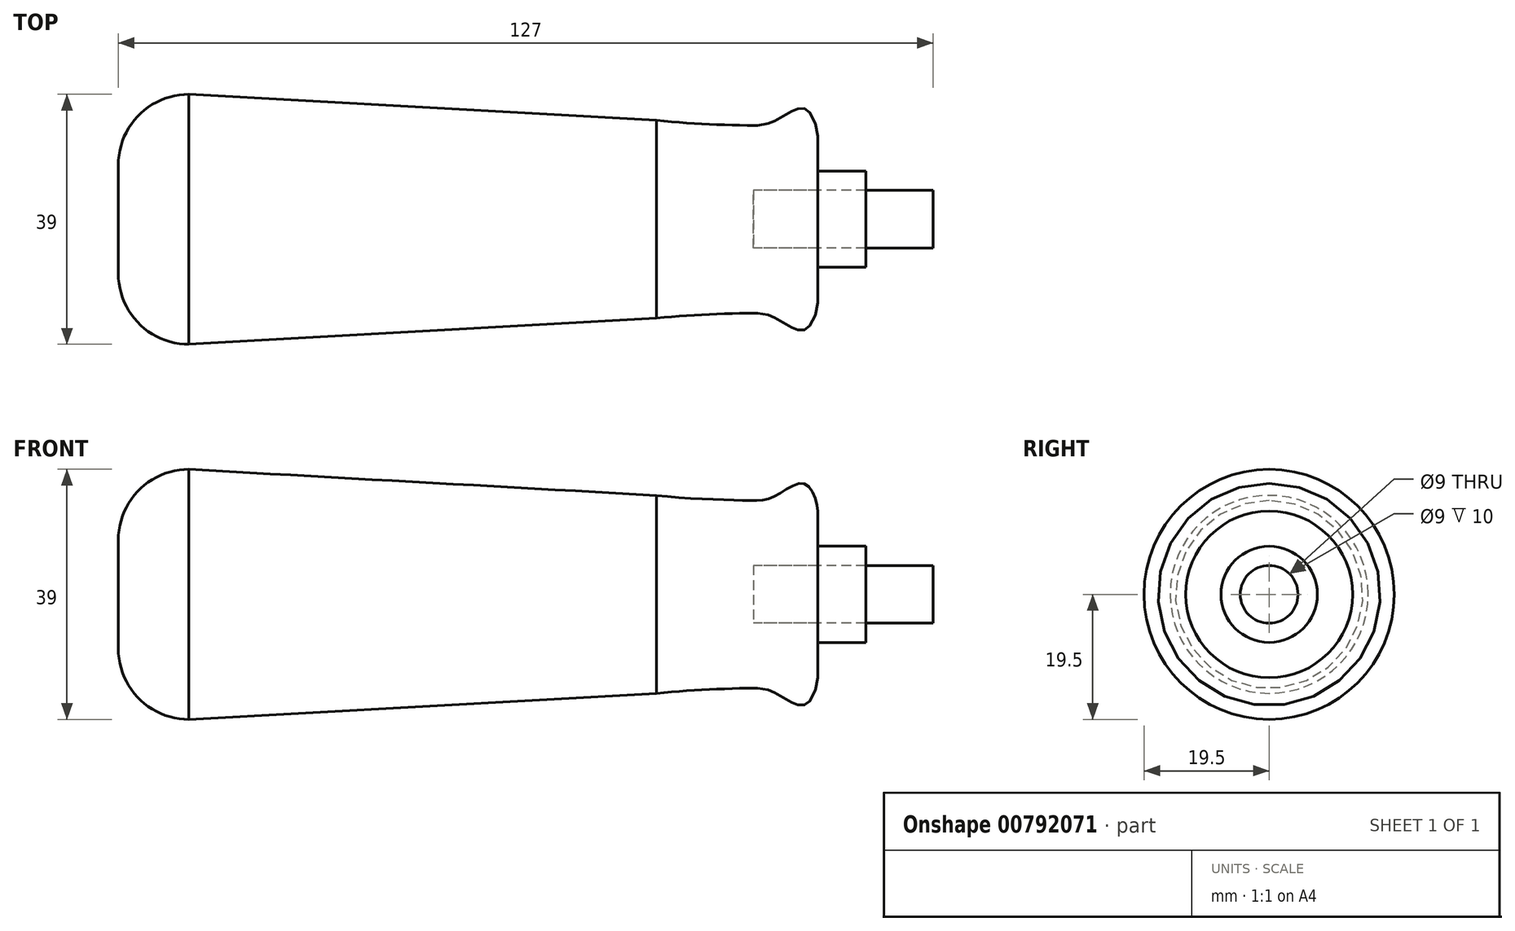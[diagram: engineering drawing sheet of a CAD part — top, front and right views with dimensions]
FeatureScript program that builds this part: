
annotation { "Feature Type Name" : "Feature", "Feature Type Description" : "" }
export const myFeature = defineFeature(function(context is Context, id is Id, definition is map)
    precondition{}
    {
        {
            var Q0;
            Q0=qCreatedBy(makeId("Front.planeOp"),FACE);
            var sketch = newSketch(context, id + "F0", { "sketchPlane" : qUnion([Q0])});
            skLineSegment(sketch, "E0", {"start": v(0, 0) * mm, "end": v(126, 0) * mm});
            skPoint(sketch, "E1", {"position": v(11, 0) * mm});
            skLineSegment(sketch, "E2", {"start": v(11, 19.5) * mm, "end": v(83.89, 15.43) * mm});
            skLineSegment(sketch, "E3", {"start": v(11, 0) * mm, "end": v(11, 26.57) * mm, "construction": true});
            skLineSegment(sketch, "E4", {"start": v(-24.26, 0) * mm, "end": v(99, 0) * mm, "construction": true});
            skLineSegment(sketch, "E5", {"start": v(109, 13) * mm, "end": v(109, 4.5) * mm});
            skLineSegment(sketch, "E6", {"start": v(109, 4.5) * mm, "end": v(99, 4.5) * mm});
            skLineSegment(sketch, "E7", {"start": v(99, 4.5) * mm, "end": v(99, 0) * mm});
            skPoint(sketch, "E8.orphan", {"position": v(109, 0) * mm});
            skLineSegment(sketch, "E9.trimOffspring", {"start": v(109, 0) * mm, "end": v(151.94, 0) * mm, "construction": true});
            skLineSegment(sketch, "E10", {"start": v(0, 0) * mm, "end": v(0, 8.5) * mm});
            skArc(sketch, "E11", {"start": v(0, 8.5) * mm, "mid": v(3.22, 16.28) * mm, "end": v(11, 19.5) * mm});
            skFitSpline(sketch, "E12", {"points": [v(83.89, 15.43) * mm, v(97.67, 14.64) * mm, v(102.34, 15.35) * mm, v(107.08, 17.22) * mm, v(109, 13) * mm], "startDerivative": vector(38.5, -4.28) * mm, "endDerivative": vector(1.14, -17.09) * mm});
            skSolve(sketch);
        }
        {
            var Q0;
            Q0=qSketchRegion(id+"F0",true);
            var Q1;
            Q1=sQuery(id+"F0.wireOp",EDGE,"E9.trimOffspring");
            revolve(context, id + "F1", {"entities" : qUnion([Q0]), "axis" : qUnion([Q1]), "revolveType" : RevolveType.FULL});
        }
        {
            var Q0;
            Q0=qCreatedBy(makeId("Front.planeOp"),FACE);
            var sketch = newSketch(context, id + "F2", { "sketchPlane" : qUnion([Q0])});
            skLineSegment(sketch, "E13", {"start": v(109, 4.5) * mm, "end": v(116.5, 4.5) * mm});
            skLineSegment(sketch, "E14", {"start": v(116.5, 4.5) * mm, "end": v(116.5, 7.5) * mm});
            skLineSegment(sketch, "E15", {"start": v(116.5, 7.5) * mm, "end": v(109, 7.5) * mm});
            skLineSegment(sketch, "E16", {"start": v(109, 7.5) * mm, "end": v(109, 4.5) * mm});
            skSolve(sketch);
        }
        {
            var Q0;
            Q0=makeQuery(id+"F2.imprint","IMPRINT",FACE,{"disambiguationData":[TD([[makeQuery(id+"F2.imprint","IMPRINT",EDGE,{"derivedFrom":sQuery(id+"F2.wireOp",EDGE,"E13")}),1.0]])]});
            var Q1;
            Q1=sQuery(id+"F0.wireOp",EDGE,"E9.trimOffspring");
            revolve(context, id + "F3", {"entities" : qUnion([Q0]), "axis" : qUnion([Q1]), "revolveType" : RevolveType.FULL});
        }
        {
            var Q0;
            Q0=makeQuery(id+"F1.opRevolve","SWEPT_FACE",FACE,{"disambiguationData":[OSD([sQuery(id+"F0.wireOp",EDGE,"E7")])]});
            var sketch = newSketch(context, id + "F4", { "sketchPlane" : qUnion([Q0])});
            skCircle(sketch, "E17.0", {"center": v(0, 0) * mm, "radius": 4.5 * mm});
            skSolve(sketch);
        }
        {
            var Q0;
            Q0=qSketchRegion(id+"F4",true);
            extrude(context, id + "F5", {"entities" : qUnion([Q0]), "depth" : 28 * mm, "offsetDistance" : 25 * mm});
        }
    });
